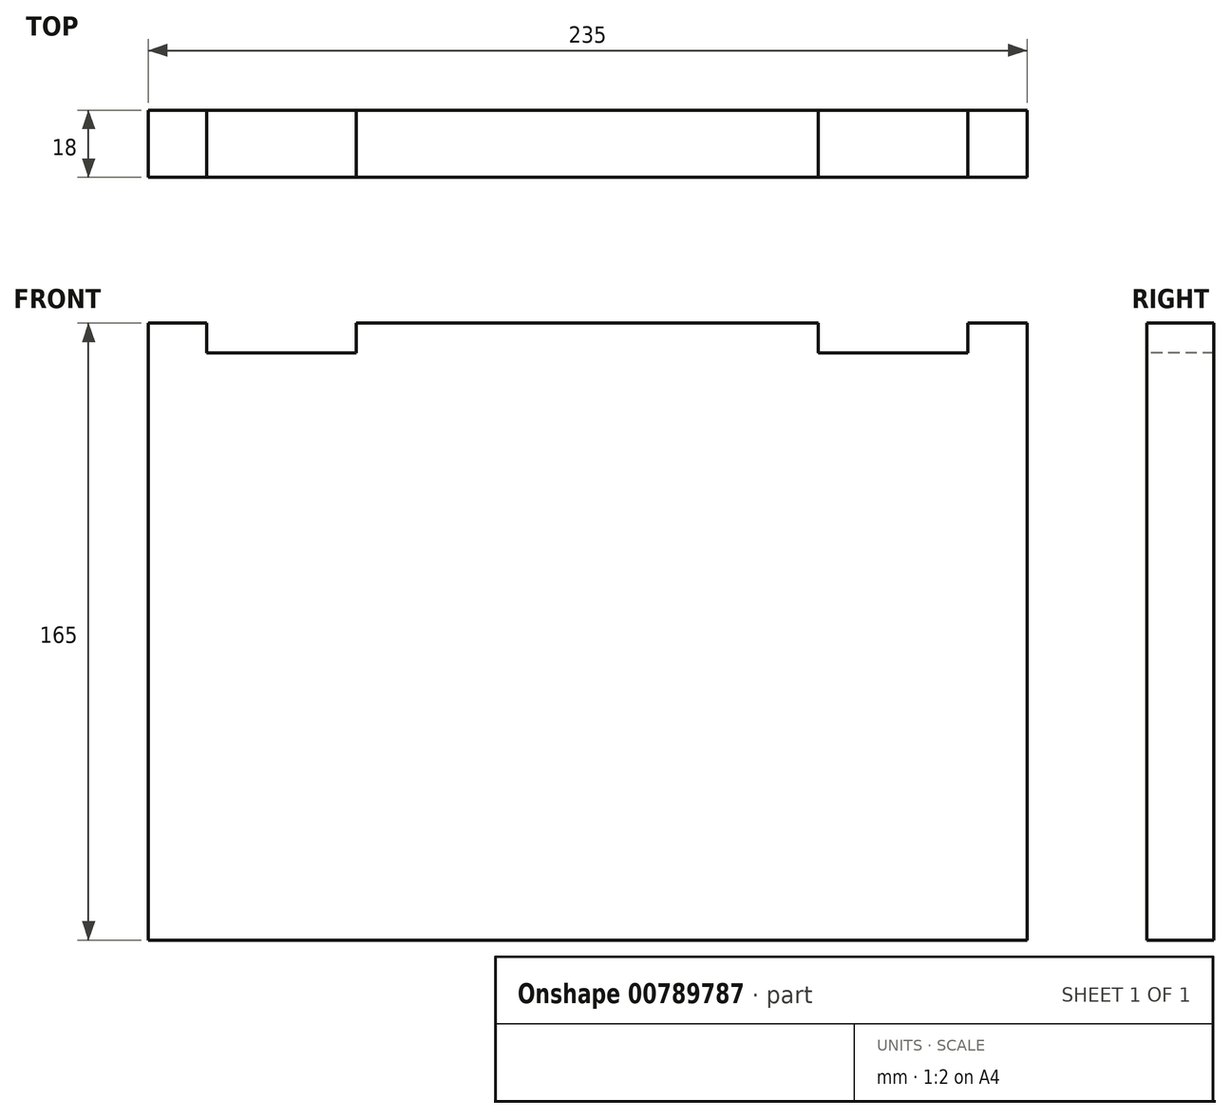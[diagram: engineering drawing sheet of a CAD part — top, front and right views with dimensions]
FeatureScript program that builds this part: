
annotation { "Feature Type Name" : "Feature", "Feature Type Description" : "" }
export const myFeature = defineFeature(function(context is Context, id is Id, definition is map)
    precondition{}
    {
        {
            var Q0;
            Q0=qCreatedBy(makeId("Front.planeOp"),FACE);
            var sketch = newSketch(context, id + "F0", { "sketchPlane" : qUnion([Q0])});
            skLineSegment(sketch, "E0.bottom", {"start": v(-112.55, 94.19) * mm, "end": v(122.45, 94.19) * mm});
            skLineSegment(sketch, "E0.top", {"start": v(-112.55, -70.81) * mm, "end": v(122.45, -70.81) * mm});
            skLineSegment(sketch, "E0.left", {"start": v(-112.55, 94.19) * mm, "end": v(-112.55, -70.81) * mm});
            skLineSegment(sketch, "E0.right", {"start": v(122.45, 94.19) * mm, "end": v(122.45, -70.81) * mm});
            skSolve(sketch);
        }
        {
            var Q0;
            Q0 = qSketchRegion(id + "F0", true);
            extrude(context, id + "F1", {"entities" : qUnion([Q0]), "depth" : 18 * mm, "offsetDistance" : 25 * mm});
        }
        {
            var Q0;
            Q0=makeQuery(id+"F1.opExtrude","SWEPT_FACE",FACE,{"disambiguationData":[OSD([sQuery(id+"F0.wireOp",EDGE,"E0.bottom")])]});
            var sketch = newSketch(context, id + "F2", { "sketchPlane" : qUnion([Q0])});
            skLineSegment(sketch, "E1.bottom", {"start": v(106.59, 0) * mm, "end": v(66.59, 0) * mm});
            skLineSegment(sketch, "E1.top", {"start": v(106.59, -18) * mm, "end": v(66.59, -18) * mm});
            skLineSegment(sketch, "E1.left", {"start": v(106.59, 0) * mm, "end": v(106.59, -18) * mm});
            skLineSegment(sketch, "E1.right", {"start": v(66.59, 0) * mm, "end": v(66.59, -18) * mm});
            skSolve(sketch);
        }
        {
            var Q0;
            Q0 = qSketchRegion(id + "F2", true);
            extrude(context, id + "F3", {"entities" : qUnion([Q0]), "operationType" : NewBodyOperationType.REMOVE, "oppositeDirection" : true, "depth" : 8 * mm, "offsetDistance" : 25 * mm});
        }
        {
            var Q0;
            {var subQ1=sQuery(id+"F0.wireOp",EDGE,"E0.left");var subQ3=sQuery(id+"F0.wireOp",EDGE,"E0.bottom");Q0=makeQuery(id+"F3.boolean.opBoolean","SPLIT",FACE,{"disambiguationData":[TD([makeQuery(id+"F1.opExtrude","SWEPT_FACE",FACE,{"disambiguationData":[OSD([subQ1])]})])],"derivedFrom":makeQuery(id+"F1.opExtrude","SWEPT_FACE",FACE,{"disambiguationData":[OSD([subQ3])]})});}
            var sketch = newSketch(context, id + "F4", { "sketchPlane" : qUnion([Q0])});
            skLineSegment(sketch, "E2.bottom", {"start": v(-96.96, 0) * mm, "end": v(-56.96, 0) * mm});
            skLineSegment(sketch, "E2.top", {"start": v(-96.96, -18) * mm, "end": v(-56.96, -18) * mm});
            skLineSegment(sketch, "E2.left", {"start": v(-96.96, 0) * mm, "end": v(-96.96, -18) * mm});
            skLineSegment(sketch, "E2.right", {"start": v(-56.96, 0) * mm, "end": v(-56.96, -18) * mm});
            skSolve(sketch);
        }
        {
            var Q0;
            Q0 = qSketchRegion(id + "F4", true);
            extrude(context, id + "F5", {"entities" : qUnion([Q0]), "operationType" : NewBodyOperationType.REMOVE, "oppositeDirection" : true, "depth" : 8 * mm, "offsetDistance" : 25 * mm});
        }
    });
